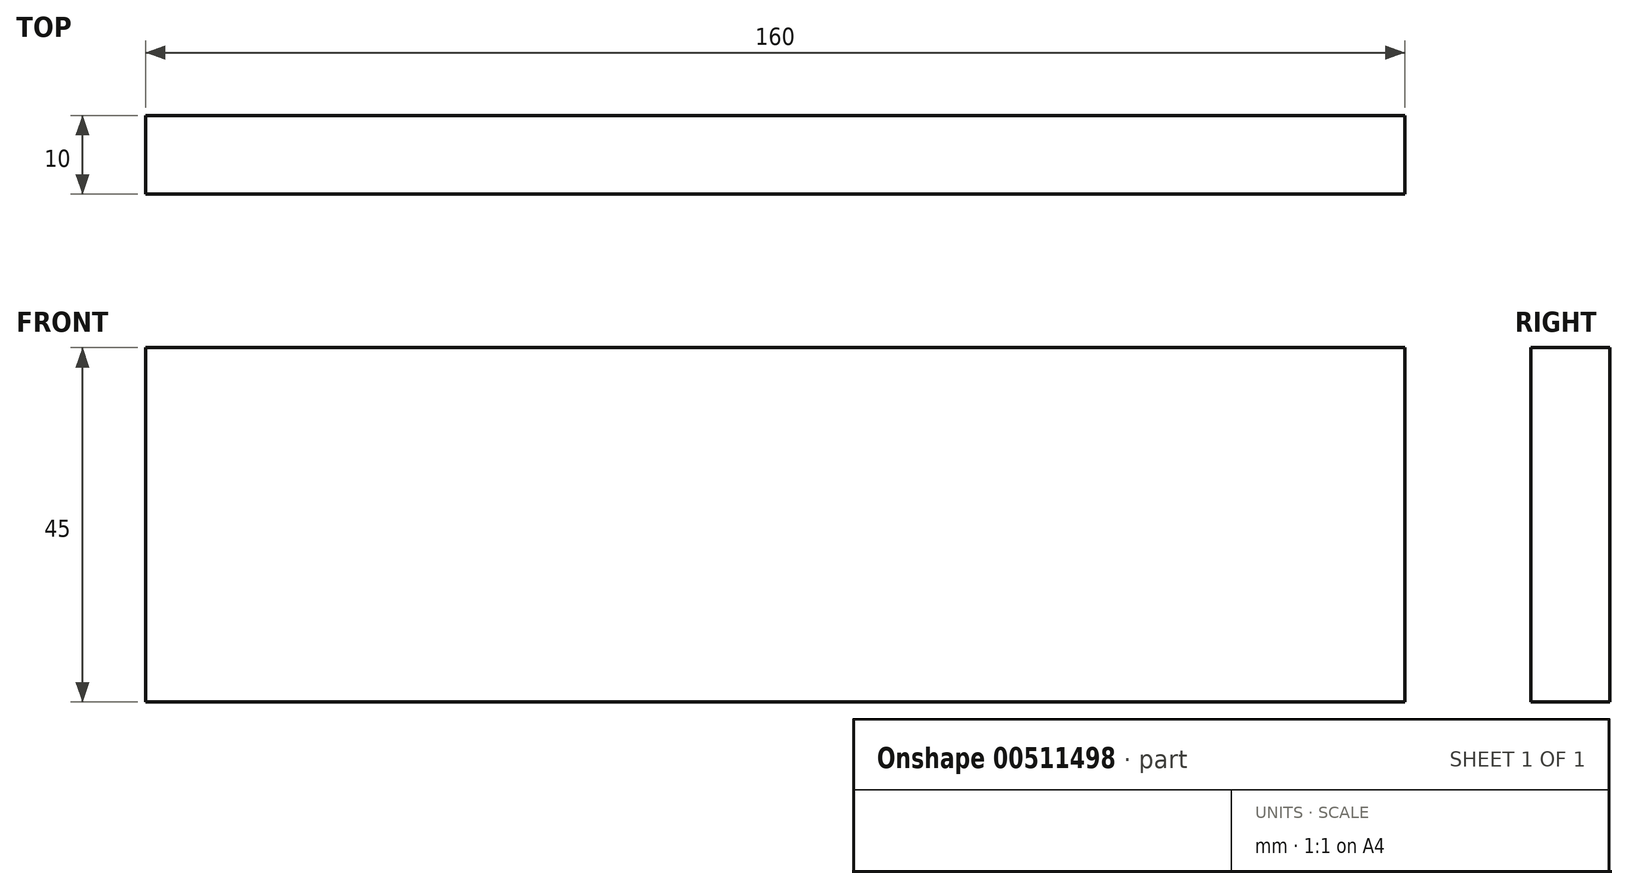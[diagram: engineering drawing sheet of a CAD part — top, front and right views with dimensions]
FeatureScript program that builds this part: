
annotation { "Feature Type Name" : "Feature", "Feature Type Description" : "" }
export const myFeature = defineFeature(function(context is Context, id is Id, definition is map)
    precondition{}
    {
        {
            var Q0;
            Q0=qCreatedBy(makeId("Front.planeOp"),FACE);
            var sketch = newSketch(context, id + "F0", { "sketchPlane" : qUnion([Q0])});
            skLineSegment(sketch, "E0.bottom", {"start": v(80, -22.5) * mm, "end": v(-80, -22.5) * mm});
            skLineSegment(sketch, "E0.top", {"start": v(80, 22.5) * mm, "end": v(-80, 22.5) * mm});
            skLineSegment(sketch, "E0.left", {"start": v(80, -22.5) * mm, "end": v(80, 22.5) * mm});
            skLineSegment(sketch, "E0.right", {"start": v(-80, -22.5) * mm, "end": v(-80, 22.5) * mm});
            skPoint(sketch, "E0.middle", {"position": v(0, 0) * mm});
            skSolve(sketch);
        }
        {
            var Q0;
            Q0=makeQuery(id+"F0.imprint","IMPRINT",FACE,{"disambiguationData":[TD([[makeQuery(id+"F0.imprint","IMPRINT",EDGE,{"derivedFrom":sQuery(id+"F0.wireOp",EDGE,"E0.bottom")}),-1.0]])]});
            extrude(context, id + "F1", {"entities" : qUnion([Q0]), "depth" : 10 * mm});
        }
    });
